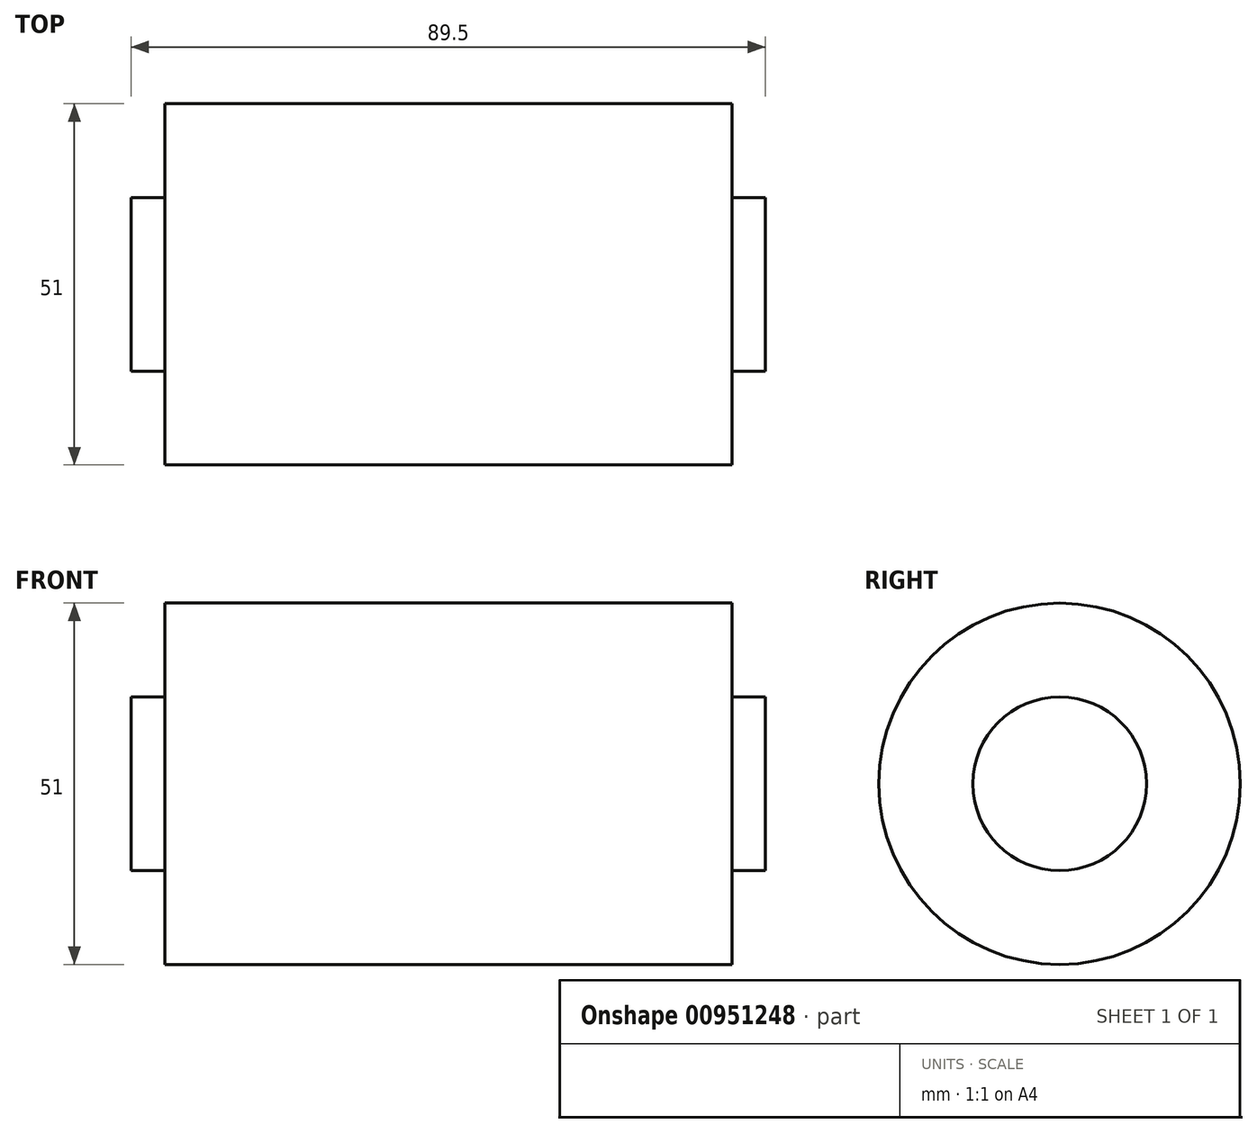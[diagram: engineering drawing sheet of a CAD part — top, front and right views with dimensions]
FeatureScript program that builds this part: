
annotation { "Feature Type Name" : "Feature", "Feature Type Description" : "" }
export const myFeature = defineFeature(function(context is Context, id is Id, definition is map)
    precondition{}
    {
        {
            var Q0;
            Q0=qCreatedBy(makeId("Right.planeOp"),FACE);
            var sketch = newSketch(context, id + "F0", { "sketchPlane" : qUnion([Q0])});
            skCircle(sketch, "E0.0", {"center": v(0, 0) * mm, "radius": 25.5 * mm});
            skCircle(sketch, "E0.1", {"center": v(0, 0) * mm, "radius": 12.75 * mm, "construction": true});
            skCircle(sketch, "E1.0", {"center": v(0, 0) * mm, "radius": 12.25 * mm});
            skSolve(sketch);
        }
        {
            var Q0;
            Q0=makeQuery(id+"F0.imprint","IMPRINT",FACE,{"disambiguationData":[TD([[makeQuery(id+"F0.imprint","IMPRINT",EDGE,{"derivedFrom":sQuery(id+"F0.wireOp",EDGE,"E0.0")}),1.0]])]});
            extrude(context, id + "F1", {"entities" : qUnion([Q0]), "endBound" : BoundingType.SYMMETRIC, "depth" : 80 * mm, "offsetDistance" : 25 * mm});
        }
        {
            var Q0;
            Q0=makeQuery(id+"F0.imprint","IMPRINT",FACE,{"disambiguationData":[TD([[makeQuery(id+"F0.imprint","IMPRINT",EDGE,{"derivedFrom":sQuery(id+"F0.wireOp",EDGE,"E1.0")}),1.0]])]});
            extrude(context, id + "F2", {"entities" : qUnion([Q0]), "operationType" : NewBodyOperationType.ADD, "endBound" : BoundingType.SYMMETRIC, "depth" : 89.5 * mm, "offsetDistance" : 25 * mm});
        }
    });
